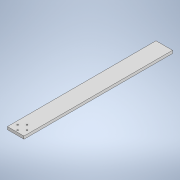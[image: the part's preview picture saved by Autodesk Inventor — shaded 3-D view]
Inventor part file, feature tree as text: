
AUTODESK INVENTOR PART (.ipt)
format: ipt  version: 2022 (Build 260153000, 153)  size: 114,688 bytes
history: native  units: mm
features: sketch x3, hole x2, other x1, extrude x1
ambient origin geometry x8: Origin, YZ Plane, XZ Plane, XY Plane, X Axis, Y Axis, Z Axis, Center Point
bodies: Body1 (feature_tree), Body2 (feature_tree)
feature tree (7):
  other  "ソリッド1"
  extrude  "押し出し1"  Depth=270.0mm
  hole  "穴1"  [1 undecoded]
  hole  "穴2"  [1 undecoded]
  sketch  "スケッチ1"
  sketch  "スケッチ2"
  sketch  "スケッチ3"
note: 2 required parameter values undecoded (feature->parameter linkage not recoverable at this tier; creation-order binding heuristic only, values carry confidence <= 0.55)
